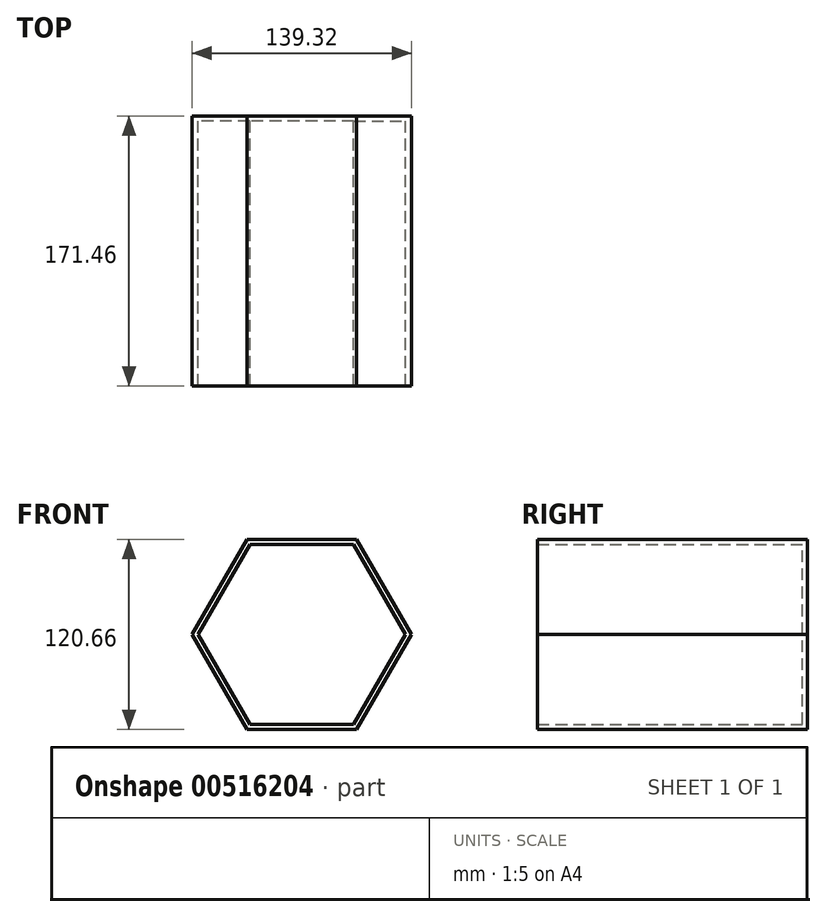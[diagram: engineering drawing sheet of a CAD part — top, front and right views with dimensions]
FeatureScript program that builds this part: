
annotation { "Feature Type Name" : "Feature", "Feature Type Description" : "" }
export const myFeature = defineFeature(function(context is Context, id is Id, definition is map)
    precondition{}
    {
        {
            var Q0;
            Q0=qCreatedBy(makeId("Front.planeOp"),FACE);
            var sketch = newSketch(context, id + "F0", { "sketchPlane" : qUnion([Q0])});
            skCircle(sketch, "E0.cCircle", {"center": v(0, 0) * mm, "radius": 60.33 * mm, "construction": true});
            skLineSegment(sketch, "E0.0", {"start": v(-34.83, 60.33) * mm, "end": v(34.83, 60.33) * mm});
            skLineSegment(sketch, "E0.1", {"start": v(34.83, 60.32) * mm, "end": v(69.66, 0) * mm});
            skLineSegment(sketch, "E0.2", {"start": v(69.66, 0) * mm, "end": v(34.83, -60.32) * mm});
            skLineSegment(sketch, "E0.3", {"start": v(34.83, -60.33) * mm, "end": v(-34.83, -60.33) * mm});
            skLineSegment(sketch, "E0.4", {"start": v(-34.83, -60.33) * mm, "end": v(-69.66, 0) * mm});
            skLineSegment(sketch, "E0.5", {"start": v(-69.66, 0) * mm, "end": v(-34.83, 60.33) * mm});
            skPoint(sketch, "E0.0.midPoint", {"position": v(0, 60.33) * mm});
            skCircle(sketch, "E1", {"center": v(0, 0) * mm, "radius": 57.15 * mm});
            skCircle(sketch, "E2.cCircle", {"center": v(0, 0) * mm, "radius": 57.15 * mm, "construction": true});
            skLineSegment(sketch, "E2.0", {"start": v(-33, 57.15) * mm, "end": v(33, 57.15) * mm});
            skLineSegment(sketch, "E2.1", {"start": v(33, 57.15) * mm, "end": v(66, 0) * mm});
            skLineSegment(sketch, "E2.2", {"start": v(66, 0) * mm, "end": v(33, -57.15) * mm});
            skLineSegment(sketch, "E2.3", {"start": v(33, -57.15) * mm, "end": v(-33, -57.15) * mm});
            skLineSegment(sketch, "E2.4", {"start": v(-33, -57.15) * mm, "end": v(-66, 0) * mm});
            skLineSegment(sketch, "E2.5", {"start": v(-66, 0) * mm, "end": v(-33, 57.15) * mm});
            skPoint(sketch, "E2.0.midPoint", {"position": v(0, 57.15) * mm});
            skSolve(sketch);
        }
        {
            var Q0;
            Q0=makeQuery(id+"F0.imprint","IMPRINT",FACE,{"disambiguationData":[TD([[makeQuery(id+"F0.imprint","IMPRINT",EDGE,{"derivedFrom":sQuery(id+"F0.wireOp",EDGE,"E0.0")}),-1.0]])]});
            extrude(context, id + "F1", {"entities" : qUnion([Q0]), "depth" : 168.27 * mm, "offsetDistance" : 25.4 * mm});
        }
        {
            var Q0;
            Q0=qCreatedBy(makeId("Front.planeOp"),FACE);
            var sketch = newSketch(context, id + "F2", { "sketchPlane" : qUnion([Q0])});
            skLineSegment(sketch, "E3.0.0", {"start": v(-69.66, 0) * mm, "end": v(-34.83, 60.33) * mm});
            skLineSegment(sketch, "E3.0.1", {"start": v(-34.83, 60.33) * mm, "end": v(34.83, 60.33) * mm});
            skLineSegment(sketch, "E3.0.2", {"start": v(34.83, 60.33) * mm, "end": v(69.66, 0) * mm});
            skLineSegment(sketch, "E3.0.3", {"start": v(69.66, 0) * mm, "end": v(34.83, -60.32) * mm});
            skLineSegment(sketch, "E3.0.4", {"start": v(34.83, -60.33) * mm, "end": v(-34.83, -60.33) * mm});
            skLineSegment(sketch, "E3.0.5", {"start": v(-34.83, -60.33) * mm, "end": v(-69.66, 0) * mm});
            skSolve(sketch);
        }
        {
            var Q0;
            Q0=makeQuery(id+"F2.imprint","IMPRINT",FACE,{"disambiguationData":[TD([[makeQuery(id+"F2.imprint","IMPRINT",EDGE,{"derivedFrom":sQuery(id+"F2.wireOp",EDGE,"E3.0.0")}),-1.0]])]});
            extrude(context, id + "F3", {"entities" : qUnion([Q0]), "operationType" : NewBodyOperationType.ADD, "oppositeDirection" : true, "depth" : 3.17 * mm, "offsetDistance" : 25.4 * mm});
        }
    });
